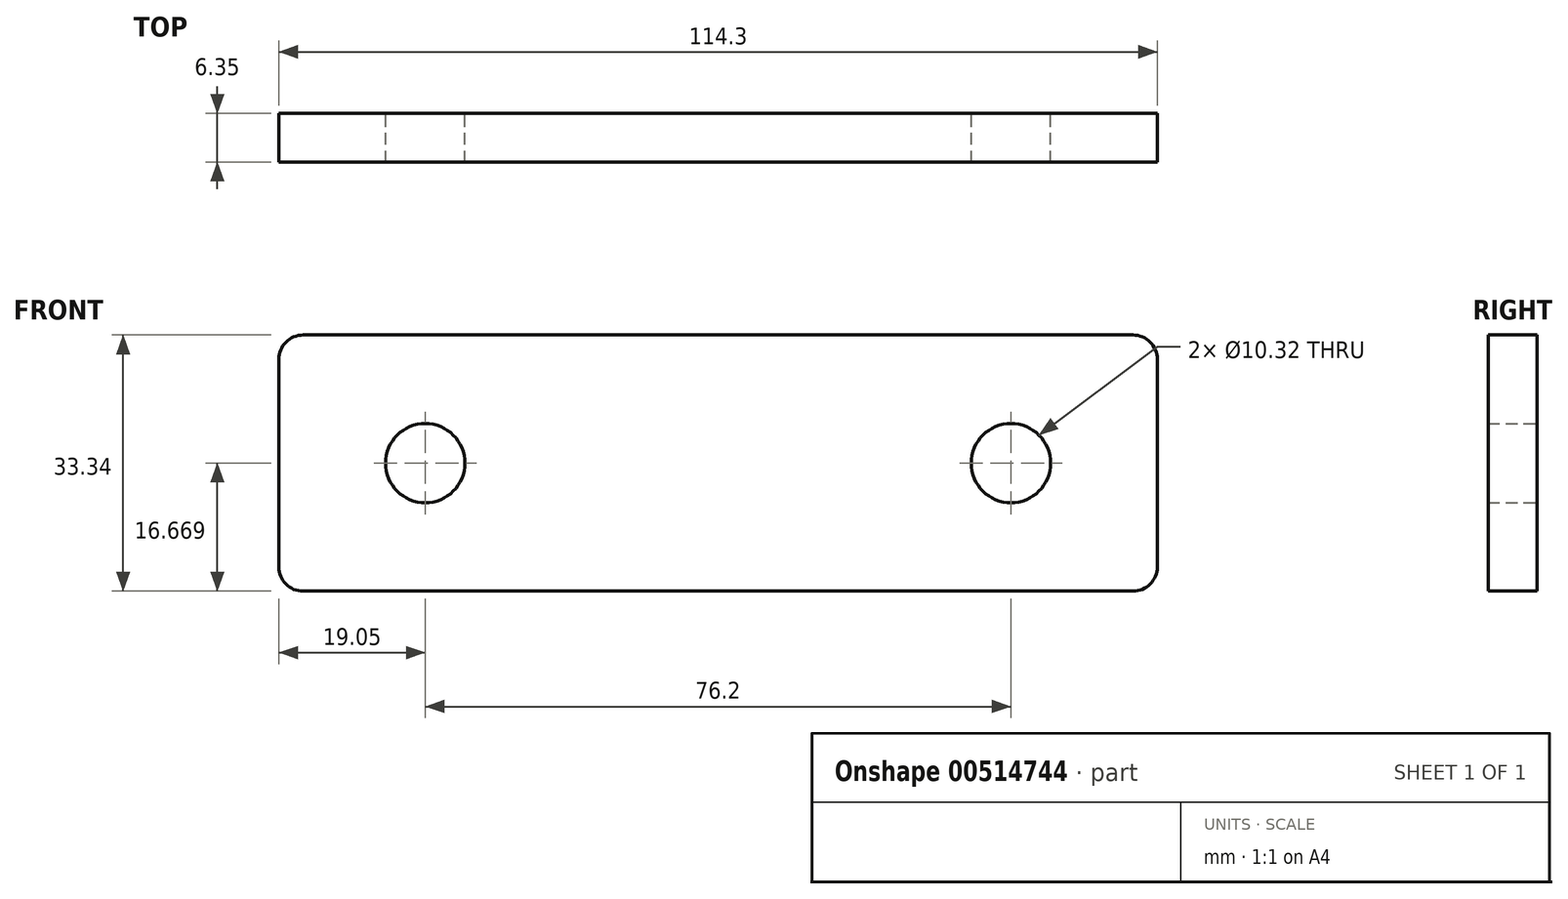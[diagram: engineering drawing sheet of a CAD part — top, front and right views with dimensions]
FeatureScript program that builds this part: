
annotation { "Feature Type Name" : "Feature", "Feature Type Description" : "" }
export const myFeature = defineFeature(function(context is Context, id is Id, definition is map)
    precondition{}
    {
        {
            var Q0;
            Q0=qCreatedBy(makeId("Front.planeOp"),FACE);
            var sketch = newSketch(context, id + "F0", { "sketchPlane" : qUnion([Q0])});
            skLineSegment(sketch, "E0.bottom", {"start": v(3.17, 0) * mm, "end": v(111.13, 0) * mm});
            skLineSegment(sketch, "E0.top", {"start": v(3.17, 33.34) * mm, "end": v(111.13, 33.34) * mm});
            skLineSegment(sketch, "E0.left", {"start": v(0, 3.18) * mm, "end": v(0, 30.16) * mm});
            skLineSegment(sketch, "E0.right", {"start": v(114.3, 3.18) * mm, "end": v(114.3, 30.16) * mm});
            skLineSegment(sketch, "E1.bottom", {"start": v(38.1, 0) * mm, "end": v(76.2, 0) * mm});
            skLineSegment(sketch, "E1.top", {"start": v(41.28, -30.15) * mm, "end": v(73.03, -30.15) * mm});
            skLineSegment(sketch, "E1.left", {"start": v(38.1, 0) * mm, "end": v(38.1, -26.97) * mm});
            skLineSegment(sketch, "E1.right", {"start": v(76.2, 0) * mm, "end": v(76.2, -26.97) * mm});
            skCircle(sketch, "E2", {"center": v(19.05, 16.67) * mm, "radius": 5.16 * mm});
            skCircle(sketch, "E3", {"center": v(95.25, 16.67) * mm, "radius": 5.16 * mm});
            skPoint(sketch, "E4.visualSharp", {"position": v(0, 33.34) * mm});
            skArc(sketch, "E4.filletArc", {"start": v(3.17, 33.34) * mm, "mid": v(0.93, 32.4) * mm, "end": v(0, 30.16) * mm});
            skPoint(sketch, "E5.visualSharp", {"position": v(0, 0) * mm});
            skArc(sketch, "E5.filletArc", {"start": v(0, 3.18) * mm, "mid": v(0.93, 0.93) * mm, "end": v(3.17, 0) * mm});
            skPoint(sketch, "E6.visualSharp", {"position": v(114.3, 0) * mm});
            skArc(sketch, "E6.filletArc", {"start": v(111.13, 0) * mm, "mid": v(113.37, 0.93) * mm, "end": v(114.3, 3.18) * mm});
            skPoint(sketch, "E7.visualSharp", {"position": v(114.3, 33.34) * mm});
            skArc(sketch, "E7.filletArc", {"start": v(114.3, 30.16) * mm, "mid": v(113.37, 32.4) * mm, "end": v(111.13, 33.34) * mm});
            skPoint(sketch, "E8.visualSharp", {"position": v(76.2, -30.15) * mm});
            skArc(sketch, "E8.filletArc", {"start": v(73.03, -30.15) * mm, "mid": v(75.27, -29.22) * mm, "end": v(76.2, -26.97) * mm});
            skPoint(sketch, "E9.visualSharp", {"position": v(38.1, -30.15) * mm});
            skArc(sketch, "E9.filletArc", {"start": v(38.1, -26.97) * mm, "mid": v(39.03, -29.22) * mm, "end": v(41.28, -30.15) * mm});
            skSolve(sketch);
        }
        {
            var Q0;
            Q0=makeQuery(id+"F0.imprint","IMPRINT",FACE,{"disambiguationData":[TD([[makeQuery(id+"F0.imprint","IMPRINT",EDGE,{"derivedFrom":sQuery(id+"F0.wireOp",EDGE,"E0.top")}),-1.0]])]});
            var Q1;
            Q1=makeQuery(id+"F0.imprint","IMPRINT",FACE,{"disambiguationData":[TD([[makeQuery(id+"F0.imprint","IMPRINT",EDGE,{"derivedFrom":sQuery(id+"F0.wireOp",EDGE,"E1.bottom")}),-1.0]])]});
            extrude(context, id + "F1", {"entities" : qUnion([Q0, Q1]), "flatOperationType" : FlatOperationType.REMOVE, "depth" : 6.35 * mm, "offsetDistance" : 25.4 * mm, "domain" : OperationDomain.MODEL});
        }
    });
